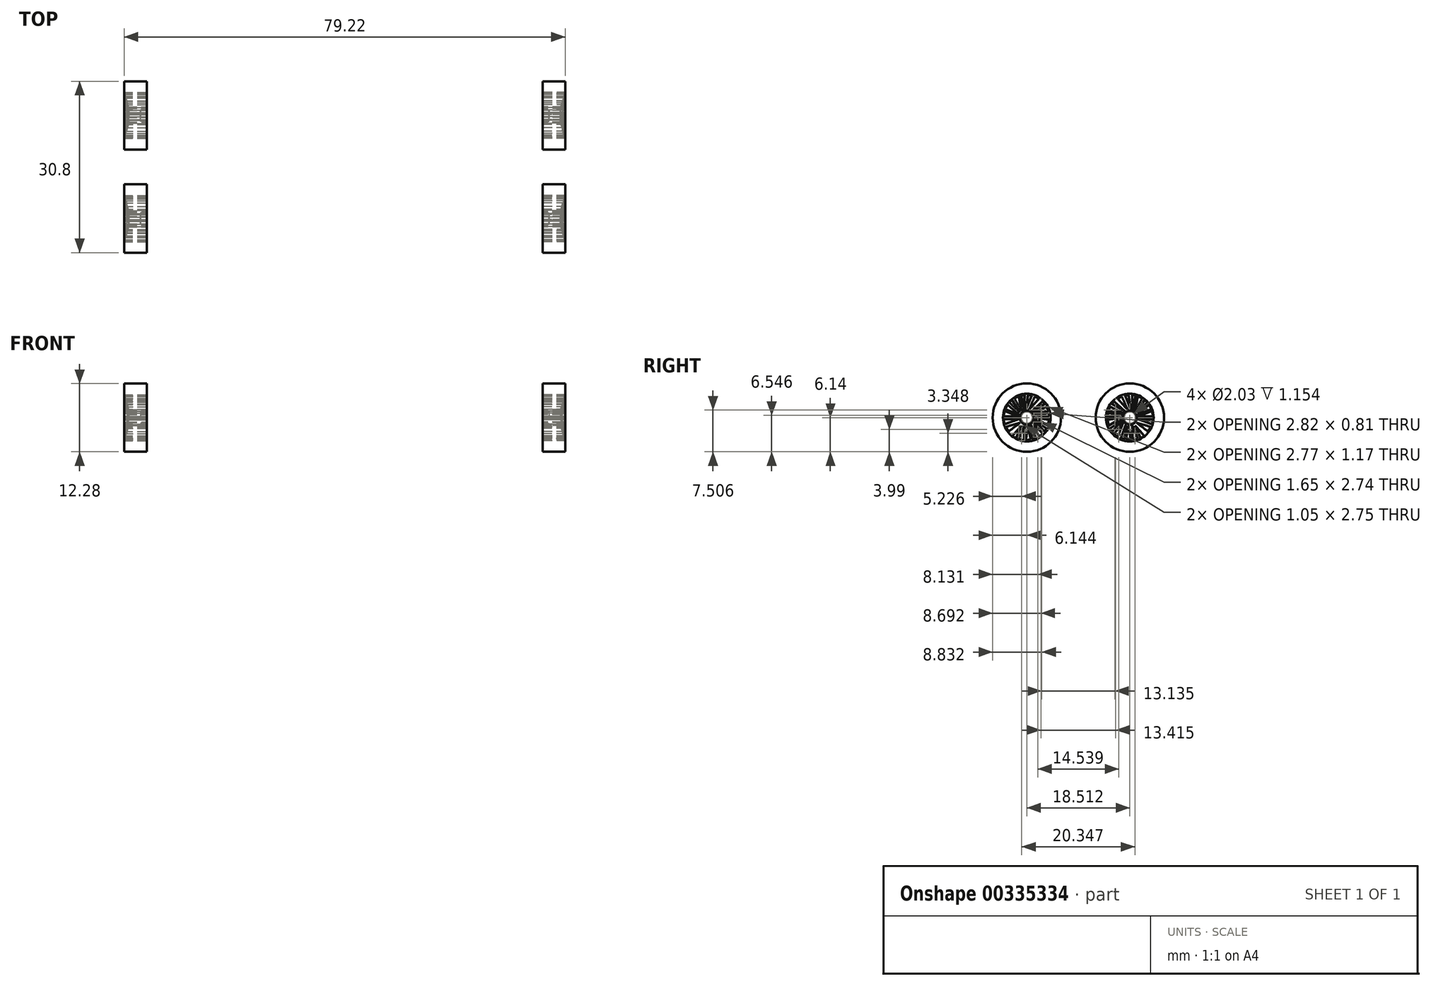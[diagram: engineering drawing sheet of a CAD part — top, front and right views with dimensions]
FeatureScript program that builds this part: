
annotation { "Feature Type Name" : "Feature", "Feature Type Description" : "" }
export const myFeature = defineFeature(function(context is Context, id is Id, definition is map)
    precondition{}
    {
        {
            var Q0;
            Q0=qCreatedBy(makeId("Top.planeOp"),FACE);
            var sketch = newSketch(context, id + "F0", { "sketchPlane" : qUnion([Q0])});
            skLineSegment(sketch, "E0", {"start": v(-38.78, 9.26) * mm, "end": v(-35.54, 9.26) * mm});
            skLineSegment(sketch, "E1", {"start": v(-38.78, 9.26) * mm, "end": v(-38.78, 10.53) * mm});
            skLineSegment(sketch, "E2", {"start": v(-38.78, 10.53) * mm, "end": v(-39.6, 13.54) * mm});
            skLineSegment(sketch, "E3", {"start": v(-39.6, 13.54) * mm, "end": v(-39.6, 15.4) * mm});
            skLineSegment(sketch, "E4", {"start": v(-39.6, 15.4) * mm, "end": v(-35.54, 15.4) * mm});
            skLineSegment(sketch, "E5", {"start": v(-35.54, 15.4) * mm, "end": v(-35.54, 9.26) * mm});
            skPoint(sketch, "E6.start.orphan", {"position": v(-38.78, 8.6) * mm});
            skPoint(sketch, "E7.end.orphan", {"position": v(-10.84, 9.26) * mm});
            skPoint(sketch, "E7.start.orphan", {"position": v(-10.84, 9.7) * mm});
            skSolve(sketch);
        }
        {
            var Q0;
            {var subQ0=sQuery(id+"F0.wireOp",EDGE,"E1");Q0=makeQuery(id+"F0.imprint","IMPRINT",FACE,{"disambiguationData":[TD([[makeQuery(id+"F0.imprint","IMPRINT",EDGE,{"derivedFrom":subQ0}),-1.0]])]});}
            var Q1;
            {var subQ4=sQuery(id+"F0.wireOp",EDGE,"CXuNwUhG-7ZFb-JLFY-qBlp-mZBsGOOG0x1J");Q1=makeQuery(id+"F0.imprint","IMPRINT",FACE,{"disambiguationData":[TD([[makeQuery(id+"F0.imprint","IMPRINT",EDGE,{"derivedFrom":subQ4}),-1.0]])]});}
            var Q2;
            Q2=sQuery(id+"F0.wireOp",EDGE,"E0");
            revolve(context, id + "F1", {"entities" : qUnion([Q0, Q1]), "axis" : qUnion([Q2]), "revolveType" : RevolveType.FULL});
        }
        {
            var Q0;
            Q0=qCreatedBy(makeId("Right.planeOp"),FACE);
            var sketch = newSketch(context, id + "F2", { "sketchPlane" : qUnion([Q0])});
            skCircle(sketch, "E8", {"center": v(9.33, 0) * mm, "radius": 4.1 * mm, "construction": true});
            skCircle(sketch, "E9", {"center": v(9.33, 0) * mm, "radius": 1.47 * mm, "construction": true});
            skLineSegment(sketch, "E10", {"start": v(12.56, -2.52) * mm, "end": v(10.47, -0.92) * mm});
            skLineSegment(sketch, "E11", {"start": v(10.47, -0.92) * mm, "end": v(13.06, -1.69) * mm});
            skLineSegment(sketch, "E12", {"start": v(13.06, -1.69) * mm, "end": v(12.56, -2.52) * mm});
            skLineSegment(sketch, "E13", {"start": v(13.25, -1.2) * mm, "end": v(10.77, -0.3) * mm});
            skLineSegment(sketch, "E14", {"start": v(10.77, -0.3) * mm, "end": v(13.42, -0.3) * mm});
            skLineSegment(sketch, "E15", {"start": v(13.42, -0.3) * mm, "end": v(13.25, -1.2) * mm});
            skLineSegment(sketch, "E16", {"start": v(13.42, 0.22) * mm, "end": v(10.78, 0.22) * mm});
            skLineSegment(sketch, "E17", {"start": v(10.78, 0.22) * mm, "end": v(13.25, 1.2) * mm});
            skLineSegment(sketch, "E18", {"start": v(13.25, 1.2) * mm, "end": v(13.42, 0.22) * mm});
            skLineSegment(sketch, "E19", {"start": v(13.13, 1.53) * mm, "end": v(10.69, 0.56) * mm});
            skLineSegment(sketch, "E20", {"start": v(10.69, 0.56) * mm, "end": v(12.7, 2.32) * mm});
            skLineSegment(sketch, "E21", {"start": v(12.7, 2.32) * mm, "end": v(13.13, 1.53) * mm});
            skLineSegment(sketch, "E22", {"start": v(10.5, 0.9) * mm, "end": v(12.38, 2.74) * mm});
            skLineSegment(sketch, "E23", {"start": v(12.38, 2.74) * mm, "end": v(11.92, 3.18) * mm});
            skLineSegment(sketch, "E24", {"start": v(11.92, 3.18) * mm, "end": v(10.5, 0.9) * mm});
            skLineSegment(sketch, "E25", {"start": v(10.69, 3.86) * mm, "end": v(10.19, 1.19) * mm});
            skLineSegment(sketch, "E26", {"start": v(10.19, 1.19) * mm, "end": v(11.5, 3.48) * mm});
            skLineSegment(sketch, "E27", {"start": v(11.5, 3.48) * mm, "end": v(10.69, 3.86) * mm});
            skLineSegment(sketch, "E28", {"start": v(9.78, 1.4) * mm, "end": v(10.26, 3.99) * mm});
            skLineSegment(sketch, "E29", {"start": v(10.26, 3.99) * mm, "end": v(9.65, 4.08) * mm});
            skLineSegment(sketch, "E30", {"start": v(9.65, 4.08) * mm, "end": v(9.78, 1.4) * mm});
            skLineSegment(sketch, "E31", {"start": v(9.41, 1.46) * mm, "end": v(9.02, 4.08) * mm});
            skLineSegment(sketch, "E32", {"start": v(9.02, 4.08) * mm, "end": v(8.39, 3.99) * mm});
            skLineSegment(sketch, "E33", {"start": v(8.39, 3.99) * mm, "end": v(9.41, 1.46) * mm});
            skLineSegment(sketch, "E34", {"start": v(8.89, 1.4) * mm, "end": v(7.82, 3.8) * mm});
            skLineSegment(sketch, "E35", {"start": v(7.82, 3.8) * mm, "end": v(7.07, 3.4) * mm});
            skLineSegment(sketch, "E36", {"start": v(7.07, 3.4) * mm, "end": v(8.89, 1.4) * mm});
            skLineSegment(sketch, "E37", {"start": v(8.39, 1.12) * mm, "end": v(6.44, 2.9) * mm});
            skLineSegment(sketch, "E38", {"start": v(6.44, 2.9) * mm, "end": v(6.05, 2.44) * mm});
            skLineSegment(sketch, "E39", {"start": v(6.05, 2.44) * mm, "end": v(8.39, 1.12) * mm});
            skLineSegment(sketch, "E40", {"start": v(8.1, 0.78) * mm, "end": v(5.73, 1.95) * mm});
            skLineSegment(sketch, "E41", {"start": v(5.73, 1.95) * mm, "end": v(5.32, 1.12) * mm});
            skLineSegment(sketch, "E42", {"start": v(5.32, 1.12) * mm, "end": v(8.1, 0.78) * mm});
            skLineSegment(sketch, "E43", {"start": v(7.98, 0.56) * mm, "end": v(5.32, 0.81) * mm});
            skLineSegment(sketch, "E44", {"start": v(5.32, 0.81) * mm, "end": v(5.16, 0) * mm});
            skLineSegment(sketch, "E45", {"start": v(5.16, 0) * mm, "end": v(7.98, 0.56) * mm});
            skLineSegment(sketch, "E46", {"start": v(7.87, 0) * mm, "end": v(5.26, -0.4) * mm});
            skLineSegment(sketch, "E47", {"start": v(5.26, -0.4) * mm, "end": v(5.5, -1.42) * mm});
            skLineSegment(sketch, "E48", {"start": v(5.5, -1.42) * mm, "end": v(7.87, 0) * mm});
            skLineSegment(sketch, "E49", {"start": v(7.92, -0.4) * mm, "end": v(5.73, -1.95) * mm});
            skLineSegment(sketch, "E50", {"start": v(5.73, -1.95) * mm, "end": v(6.05, -2.53) * mm});
            skLineSegment(sketch, "E51", {"start": v(6.05, -2.53) * mm, "end": v(7.92, -0.4) * mm});
            skLineSegment(sketch, "E52", {"start": v(8.1, -0.78) * mm, "end": v(6.44, -2.9) * mm});
            skLineSegment(sketch, "E53", {"start": v(6.44, -2.9) * mm, "end": v(7.07, -3.52) * mm});
            skLineSegment(sketch, "E54", {"start": v(7.07, -3.52) * mm, "end": v(8.1, -0.78) * mm});
            skLineSegment(sketch, "E55", {"start": v(8.56, -1.24) * mm, "end": v(7.63, -3.72) * mm});
            skLineSegment(sketch, "E56", {"start": v(7.63, -3.72) * mm, "end": v(8.39, -3.8) * mm});
            skLineSegment(sketch, "E57", {"start": v(8.39, -3.8) * mm, "end": v(8.56, -1.24) * mm});
            skLineSegment(sketch, "E58", {"start": v(9.02, -1.42) * mm, "end": v(9.41, -4.03) * mm});
            skLineSegment(sketch, "E59", {"start": v(9.41, -4.03) * mm, "end": v(8.56, -3.95) * mm});
            skLineSegment(sketch, "E60", {"start": v(8.56, -3.95) * mm, "end": v(9.02, -1.42) * mm});
            skLineSegment(sketch, "E61", {"start": v(9.65, -1.42) * mm, "end": v(10.7, -3.8) * mm});
            skLineSegment(sketch, "E62", {"start": v(10.7, -3.8) * mm, "end": v(9.78, -4.17) * mm});
            skLineSegment(sketch, "E63", {"start": v(9.78, -4.17) * mm, "end": v(9.65, -1.42) * mm});
            skLineSegment(sketch, "E64", {"start": v(10.19, -1.42) * mm, "end": v(11.2, -3.72) * mm});
            skLineSegment(sketch, "E65", {"start": v(11.2, -3.72) * mm, "end": v(11.82, -3.25) * mm});
            skLineSegment(sketch, "E66", {"start": v(11.82, -3.25) * mm, "end": v(10.19, -1.42) * mm});
            skLineSegment(sketch, "E67", {"start": v(15.9, 0) * mm, "end": v(3.2, 0) * mm, "construction": true});
            skSolve(sketch);
        }
        {
            var Q0;
            Q0 = qSketchRegion(id + "F2", true);
            extrude(context, id + "F3", {"entities" : qUnion([Q0]), "operationType" : NewBodyOperationType.REMOVE, "oppositeDirection" : true, "depth" : 54.36 * mm});
        }
        {
            var Q0;
            Q0=makeQuery(id+"F1.opRevolve","SWEPT_FACE",FACE,{"disambiguationData":[OSD([sQuery(id+"F0.wireOp",EDGE,"E1")])]});
            var sketch = newSketch(context, id + "F4", { "sketchPlane" : qUnion([Q0])});
            skCircle(sketch, "E68", {"center": v(-9.26, 0) * mm, "radius": 1.02 * mm});
            skSolve(sketch);
        }
        {
            var Q0;
            Q0 = qSketchRegion(id + "F4", true);
            extrude(context, id + "F5", {"entities" : qUnion([Q0]), "operationType" : NewBodyOperationType.REMOVE, "oppositeDirection" : true, "depth" : 7.67 * mm, "hasSecondDirection" : true, "secondDirectionOppositeDirection" : true, "secondDirectionDepth" : 2.08 * mm});
        }
        {
            var Q0;
            Q0=makeQuery(id+"F1.opRevolve","SWEPT_BODY",BODY,{"disambiguationData":[OSD([sQuery(id+"F0.wireOp",EDGE,"E0"),sQuery(id+"F0.wireOp",EDGE,"E1"),sQuery(id+"F0.wireOp",EDGE,"E2"),sQuery(id+"F0.wireOp",EDGE,"E3"),sQuery(id+"F0.wireOp",EDGE,"E4"),sQuery(id+"F0.wireOp",EDGE,"E5")])]});
            var Q1;
            Q1=qCreatedBy(makeId("Front.planeOp"),FACE);
            mirror(context, id + "F6", {"entities" : qUnion([Q0]), "mirrorPlane" : qUnion([Q1])});
        }
        {
            var Q0;
            Q0=makeQuery(id+"F1.opRevolve","SWEPT_BODY",BODY,{"disambiguationData":[OSD([sQuery(id+"F0.wireOp",EDGE,"E0"),sQuery(id+"F0.wireOp",EDGE,"E1"),sQuery(id+"F0.wireOp",EDGE,"E2"),sQuery(id+"F0.wireOp",EDGE,"E3"),sQuery(id+"F0.wireOp",EDGE,"E4"),sQuery(id+"F0.wireOp",EDGE,"E5")])]});
            var Q1;
            Q1=makeQuery(id+"F6.opPattern","COPY",BODY,{"derivedFrom":makeQuery(id+"F1.opRevolve","SWEPT_BODY",BODY,{"disambiguationData":[OSD([sQuery(id+"F0.wireOp",EDGE,"E0"),sQuery(id+"F0.wireOp",EDGE,"E1"),sQuery(id+"F0.wireOp",EDGE,"E2"),sQuery(id+"F0.wireOp",EDGE,"E3"),sQuery(id+"F0.wireOp",EDGE,"E4"),sQuery(id+"F0.wireOp",EDGE,"E5")])]}),"instanceName":"1"});
            var Q2;
            Q2=qCreatedBy(makeId("Right.planeOp"),FACE);
            mirror(context, id + "F7", {"entities" : qUnion([Q0, Q1]), "mirrorPlane" : qUnion([Q2])});
        }
    });
